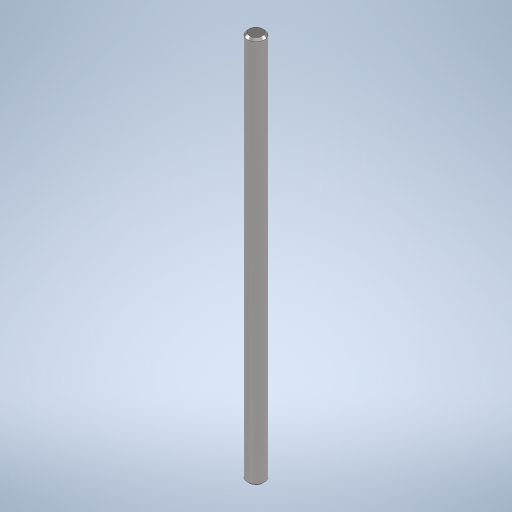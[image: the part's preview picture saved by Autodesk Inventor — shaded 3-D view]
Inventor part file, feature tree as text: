
AUTODESK INVENTOR PART (.ipt)
format: ipt  version: 2024 (Build 280153000, 153)  size: 235,008 bytes
history: native  units: mm
features: extrude x1, chamfer x1, sketch x1
ambient origin geometry x8: Origin, YZ Plane, XZ Plane, XY Plane, X Axis, Y Axis, Z Axis, Center Point
bodies: Solid1 (feature_tree)
feature tree (3):
  extrude  "Extrusion1"  Depth=360.0mm TaperAngle=0.0deg
  chamfer  "Chamfer1"  Distance=2.0mm Angle=45.0deg
  sketch  "Sketch1"  dims[d0=16.0mm d1=360.0mm d2=0.0mm d3=2.0mm d4=2.0mm d5=45.0deg]
